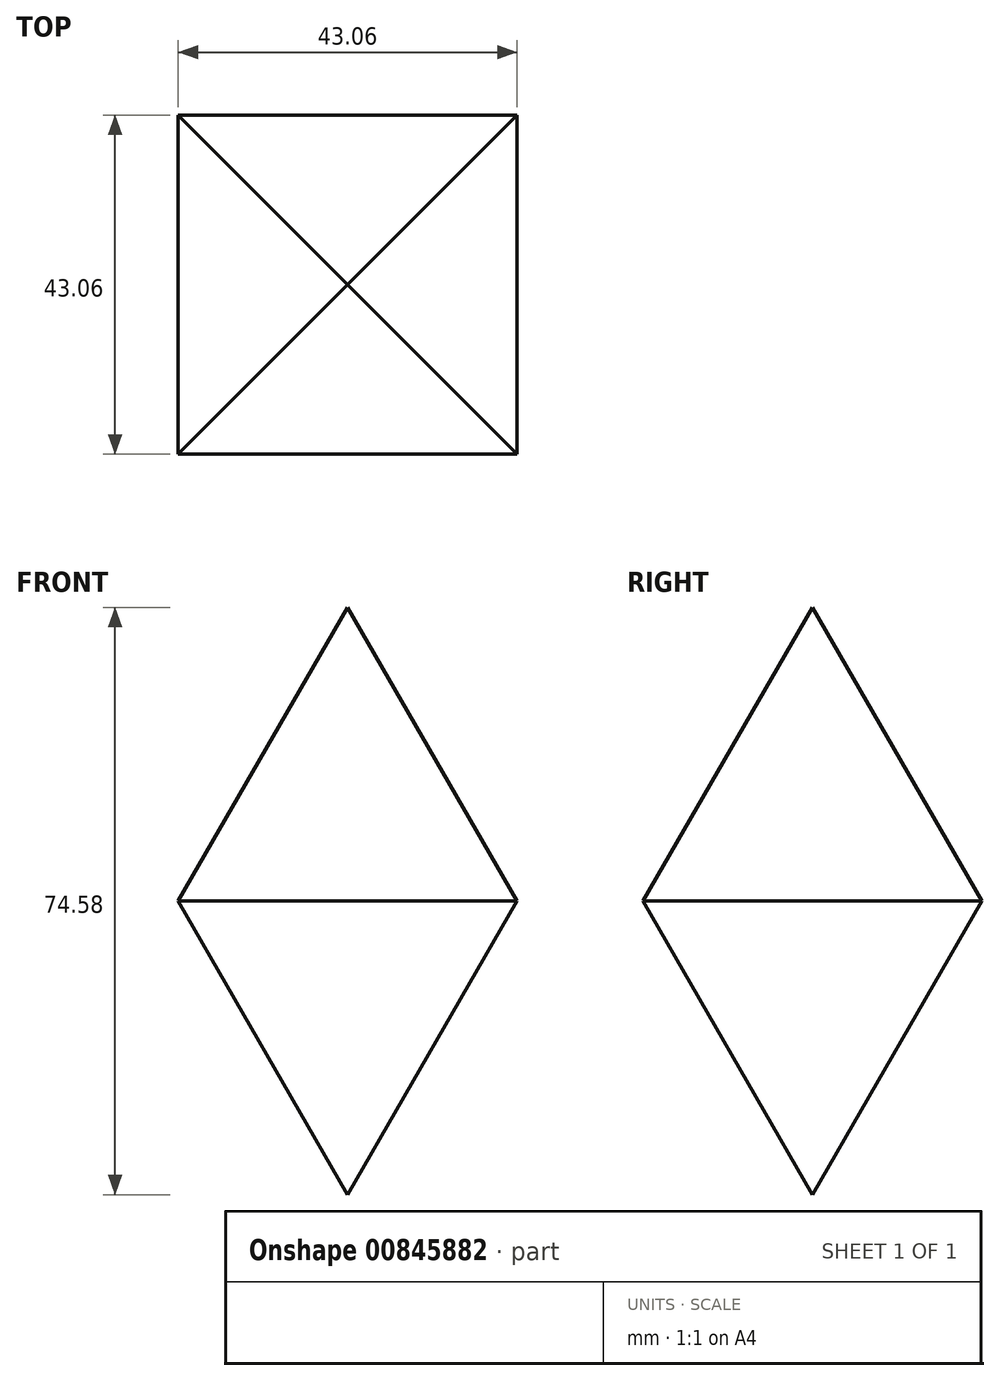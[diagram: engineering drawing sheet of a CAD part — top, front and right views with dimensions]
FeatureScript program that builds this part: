
annotation { "Feature Type Name" : "Feature", "Feature Type Description" : "" }
export const myFeature = defineFeature(function(context is Context, id is Id, definition is map)
    precondition{}
    {
        {
            var Q0;
            Q0=qCreatedBy(makeId("Top.planeOp"),FACE);
            var sketch = newSketch(context, id + "F0", { "sketchPlane" : qUnion([Q0])});
            skLineSegment(sketch, "E0.bottom", {"start": v(-64.57, 57.88) * mm, "end": v(-21.5, 57.88) * mm});
            skLineSegment(sketch, "E0.top", {"start": v(-64.57, 14.82) * mm, "end": v(-21.5, 14.82) * mm});
            skLineSegment(sketch, "E0.left", {"start": v(-64.57, 57.88) * mm, "end": v(-64.57, 14.82) * mm});
            skLineSegment(sketch, "E0.right", {"start": v(-21.5, 57.88) * mm, "end": v(-21.5, 14.82) * mm});
            skSolve(sketch);
        }
        {
            var Q0;
            Q0=makeQuery(id+"F0.imprint","IMPRINT",FACE,{"disambiguationData":[TD([[makeQuery(id+"F0.imprint","IMPRINT",EDGE,{"derivedFrom":sQuery(id+"F0.wireOp",EDGE,"E0.bottom")}),-1.0]])]});
            extrude(context, id + "F1", {"entities" : qUnion([Q0]), "depth" : 85.1 * mm, "offsetDistance" : 25.4 * mm, "hasDraft" : true, "draftAngle" : 30 * degree, "draftPullDirection" : true, "hasSecondDirection" : true, "secondDirectionOppositeDirection" : true, "secondDirectionDepth" : 41.66 * mm, "hasSecondDirectionDraft" : true, "secondDirectionDraftAngle" : 30 * degree, "secondDirectionDraftPullDirection" : true});
        }
    });
